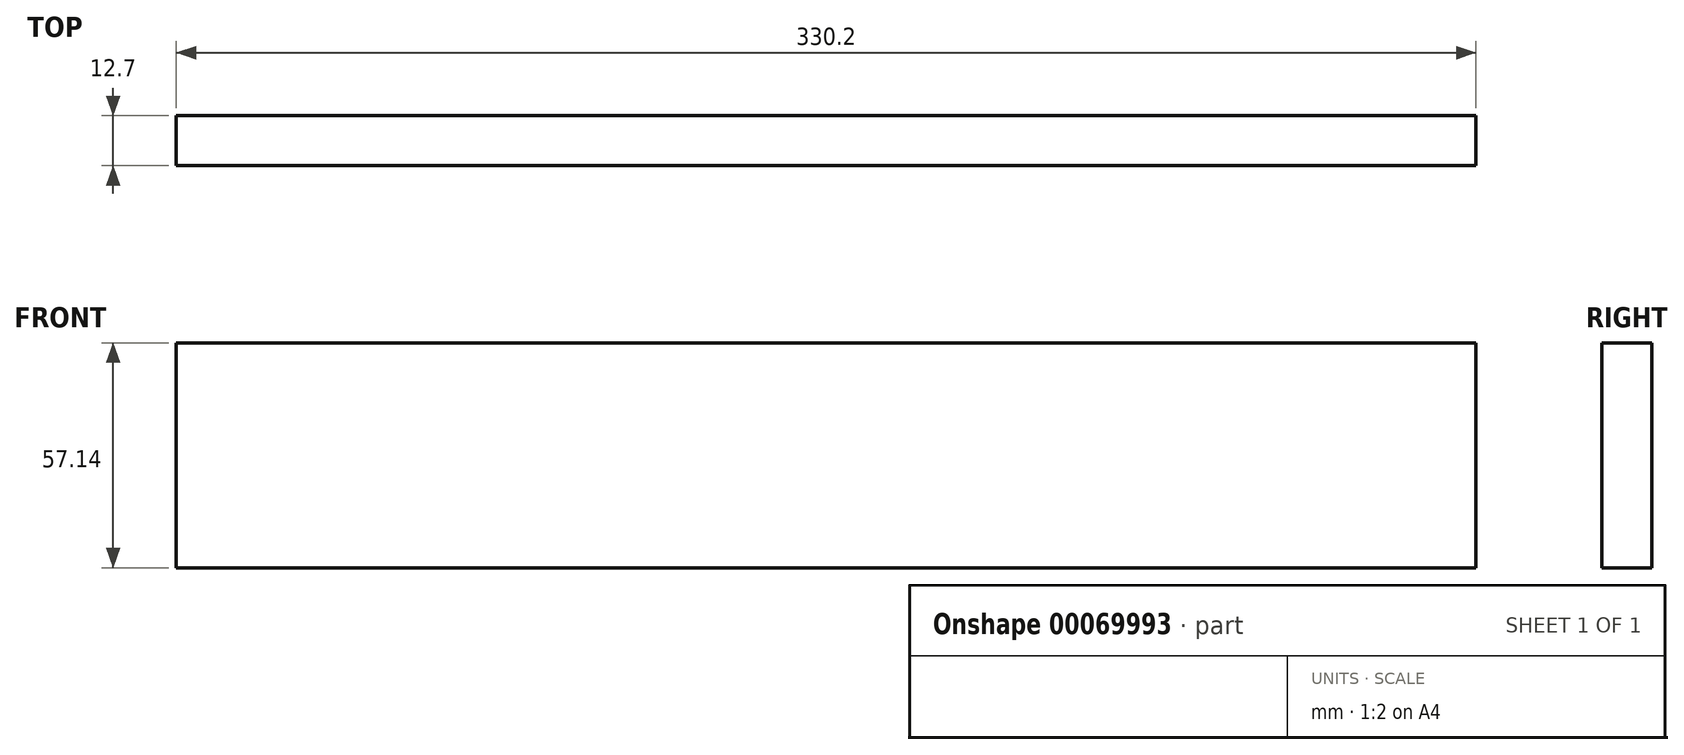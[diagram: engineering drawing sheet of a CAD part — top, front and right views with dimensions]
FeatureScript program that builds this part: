
annotation { "Feature Type Name" : "Feature", "Feature Type Description" : "" }
export const myFeature = defineFeature(function(context is Context, id is Id, definition is map)
    precondition{}
    {
        {
            var Q0;
            Q0=qCreatedBy(makeId("Front.planeOp"),FACE);
            var sketch = newSketch(context, id + "F0", { "sketchPlane" : qUnion([Q0])});
            skLineSegment(sketch, "E0.rect.bottom", {"start": v(165.1, 28.58) * mm, "end": v(-165.1, 28.58) * mm});
            skLineSegment(sketch, "E0.rect.top", {"start": v(165.1, -28.58) * mm, "end": v(-165.1, -28.58) * mm});
            skLineSegment(sketch, "E0.rect.left", {"start": v(165.1, 28.58) * mm, "end": v(165.1, -28.58) * mm});
            skLineSegment(sketch, "E0.rect.right", {"start": v(-165.1, 28.58) * mm, "end": v(-165.1, -28.58) * mm});
            skPoint(sketch, "E0.rect.middle", {"position": v(0, 0) * mm});
            skSolve(sketch);
        }
        {
            var Q0;
            Q0=makeQuery(id+"F0.imprint","IMPRINT",FACE,{"disambiguationData":[TD([[makeQuery(id+"F0.imprint","IMPRINT",EDGE,{"derivedFrom":sQuery(id+"F0.wireOp",EDGE,"E0.rect.bottom")}),1.0]])]});
            extrude(context, id + "F1", {"entities" : qUnion([Q0]), "depth" : 12.7 * mm});
        }
    });
